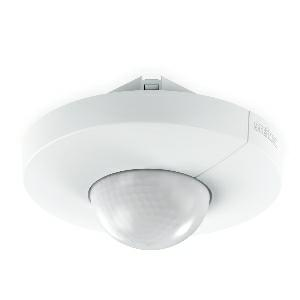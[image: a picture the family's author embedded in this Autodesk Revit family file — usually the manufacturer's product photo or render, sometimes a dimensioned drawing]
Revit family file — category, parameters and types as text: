
# Revit family: is_345_033842
name_source: partatom
category: Elektroinstallationen
revit_build: Autodesk Revit 2016 (Build: 20190508_0715(x64)
units: mm (PartAtom-declared; Revit-internal decimal feet)

## family parameters
Basisbauteil = Fläche
Beim Laden mit Abzugskörper schneiden = Nein
Bemaßung runder Anschluss = Durchmesser verwenden
Beschriftungsausrichtung beibehalten = Nein
Gemeinsam genutzt = Nein
Raumberechnungspunkt = Nein
Teiletyp = Normal

## types (1)
- IS 345
    Apparent Load = 0 VA
    Beschreibung = Type: Motion detectors; Dimensions (Ø x H): 124 x 78 mm; Mains power supply: 220 – 240 V / 50 – 60 Hz; Sensor Technology: passive infrared; Application, place: Indoors; Application, room: corridor / aisle, multi-storey / underground car park, Indoors; Installation site: ceiling; Installation: Concealed wiring; Switching zones: 280 switching zones; Electronic scalability: No; Mechanical scalability: No; Mounting height: 2,50 – 5,00 m; Optimum mounting height: 2,8 m; Detection angle: 360 °; Angle of aperture: 45 °; Sneak-by guard: Yes; Capability of masking out individual segments: Yes; Reach, radial: 12 x 6 m (72 m²); Reach, tangential: 23 x 6 m (138 m²); Twilight setting TEACH: Yes; Twilight setting: 2 – 1000 lx; Time setting: 5 sec – 15 min; Constant-lighting control: No; Basic light level function: No; Functions: Normal / test mode, Manual ON / ON-OFF; Settings via: Remote control, Potentiometers, Smart Remote; With remote control: No; Interconnection: Yes; IP-rating: IP20; Material: Plastic; Ambient temperature: -20 – 50 °C; Colour: white; Colour, RAL: 9003; Manufacturer's Warranty: 5 years; Version: PF - concealed, rd.; PU1, EAN: 4007841033842
    Height = 0 mm  [stored 0 ft]
    Hersteller = Steinel
    Length = 124 mm  [stored 0.406824 ft]
    Maximum range = 11.589 m
    ModVariant = Nein
    Modell = 033842
    Mounting Place = Ceiling
    Mounting Type = Recessed
    Number of Poles = 1
    OnlyDefault = Ja
    Power Factor = 1
    Product Name = IS 345
    Product group = Presence detector
    ProductGroupID = 4
    Protection Class = Protection class
    Protection Degree = IP 20
    RlxData = <blob elided: 156277 chars, md5=f1c8f744>
    Sensor characteristics = Stretched
    Sensor type = Passive (infrared)
    SensorDataFile = <blob elided: 5885 chars, md5=98bccc25>
    Type of entry = Motion
    Typenbild = produkt1_033842.jpg
    Typenkommentare = Product without accessories
    URL = http://relux.com
    VarID = ---
    Voltage = 0 V
    Vorgabe-Ansicht = 1800 mm
    Weight = 0.00 kg
    Width = 0 mm  [stored 0 ft]

note: [stored X ft] marks values corroborated as IEEE doubles in the binary element streams (Revit-internal decimal feet)

## geometry (parser evidence)
native form markers: Blend x4, Sweep x20
no freeform markers — native parametric forms only
